# Revit family: HL_Корпус плоского душевого лотка InFloor_HL53K.2
name_source: partatom
category: Instalační zařizovací předměty
revit_build: Autodesk Revit 2016 (Build: 20161004_0715(x64)
units: mm (PartAtom-declared; Revit-internal decimal feet)

## family parameters
Bod výpočtu místnosti = Ano
Kóta kulaté spojky = Použít průměr
Nadpis OmniClass = General Pipework and Ductwork Products
Ořezat dutým tvarem při načtení = Ne
Sdílené = Ne
Typ součásti = Normální
Vždy vertikální = Ano
Založené na pracovní rovině = Ne
Číslo OmniClass = 23.60.30.00

## types (1)
- HL_Корпус плоского душевого лотка InFloor_HL53K.2
    Cena = 0 $
    EAN = 9003076047802
    HL053_тип = HL_Решётка душевого лотка InFloor полированная_HL053P.2 : HL_Решётка душевого лотка InFloor полированная_HL053P.2_200
    Klíčová poznámka = HL53K.2
    Komentáře k typům = Корпус душевого лотка InFloor Duo, DN50
    Model = HL53K.2
    Popis = Корпус плоского душевого лотка InFloor Duo, 2x DN40
    URL = http://www.hutterer-lechner.com
    Výrobce = HL Hutterer & Lechner GmbH
    e = 450 mm  [stored 1.47638 ft]
    ВЕС = 2,95 kg
    ВЫСОТА МОНТАЖА = 90-143mm
    МАТЕРИАЛ = PP
    НОМИНАЛЬНЫЙ ДИАМЕТР = 50 mm
    ПРОИЗВОДИТЕЛЬНОСТЬ = 1,45 l/s
    ПРОПУСКНАЯ СПОСОБНОСТЬ = 0.0 m³/h
    РАЗМЕР = 2 x DN50

note: [stored X ft] marks values corroborated as IEEE doubles in the binary element streams (Revit-internal decimal feet)
